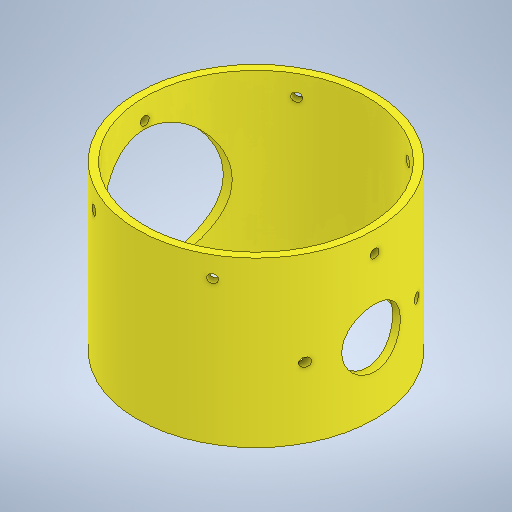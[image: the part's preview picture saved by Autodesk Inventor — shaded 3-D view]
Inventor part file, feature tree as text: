
AUTODESK INVENTOR PART (.ipt)
format: ipt  version: 2025.1 (Build 291241000, 241)  size: 310,784 bytes
history: native  units: mm
features: sketch x5, extrude x3, plane x2, hole x2, pattern_circular x1, projected_geometry x1
ambient origin geometry x8: Origin, YZ Plane, XZ Plane, XY Plane, X Axis, Y Axis, Z Axis, Center Point
bodies: Solid1 (feature_tree)
feature tree (14):
  extrude  "Extrusion1"  Depth=76.0mm
  plane  "Work Plane1"
  hole  "Hole1"  [1 undecoded]
  hole  "Hole2"  [1 undecoded]
  pattern_circular  "Circular Pattern1"  [2 undecoded]
  extrude  "Extrusion4"  Depth=60.0mm TaperAngle=360.0deg
  plane  "Work Plane2"
  extrude  "Extrusion5"  Depth=20.0mm
  sketch  "Sketch1"  dims[d0=81.0mm d1=76.0mm]
  sketch  "Sketch2"  dims[d2=56.0mm d3=0.0mm d4=40.5mm]
  projected_geometry  "Projected Loop1"
  sketch  "Sketch3"  dims[d5=24.0mm d6=19.0mm]
  sketch  "Sketch5"  dims[d7=19.0mm]
  sketch  "Sketch6"  dims[d8=3.0mm d9=6.0mm d10=4.0mm d11=2.0mm d12=90.0deg d13=9.0mm d14=0.0mm d15=7.0mm d16=3.0mm d17=6.0mm d18=4.0mm d19=2.0mm d20=90.0deg d21=3.0mm d22=0.0mm d23=60.0mm d24=360.0deg d33=20.0mm d34=24.0mm d35=4.0mm d36=0.0mm d37=-40.5mm d38=45.0mm d39=24.0mm d40=4.0mm d41=0.0mm]
note: 4 required parameter values undecoded (feature->parameter linkage not recoverable at this tier; creation-order binding heuristic only, values carry confidence <= 0.55)
